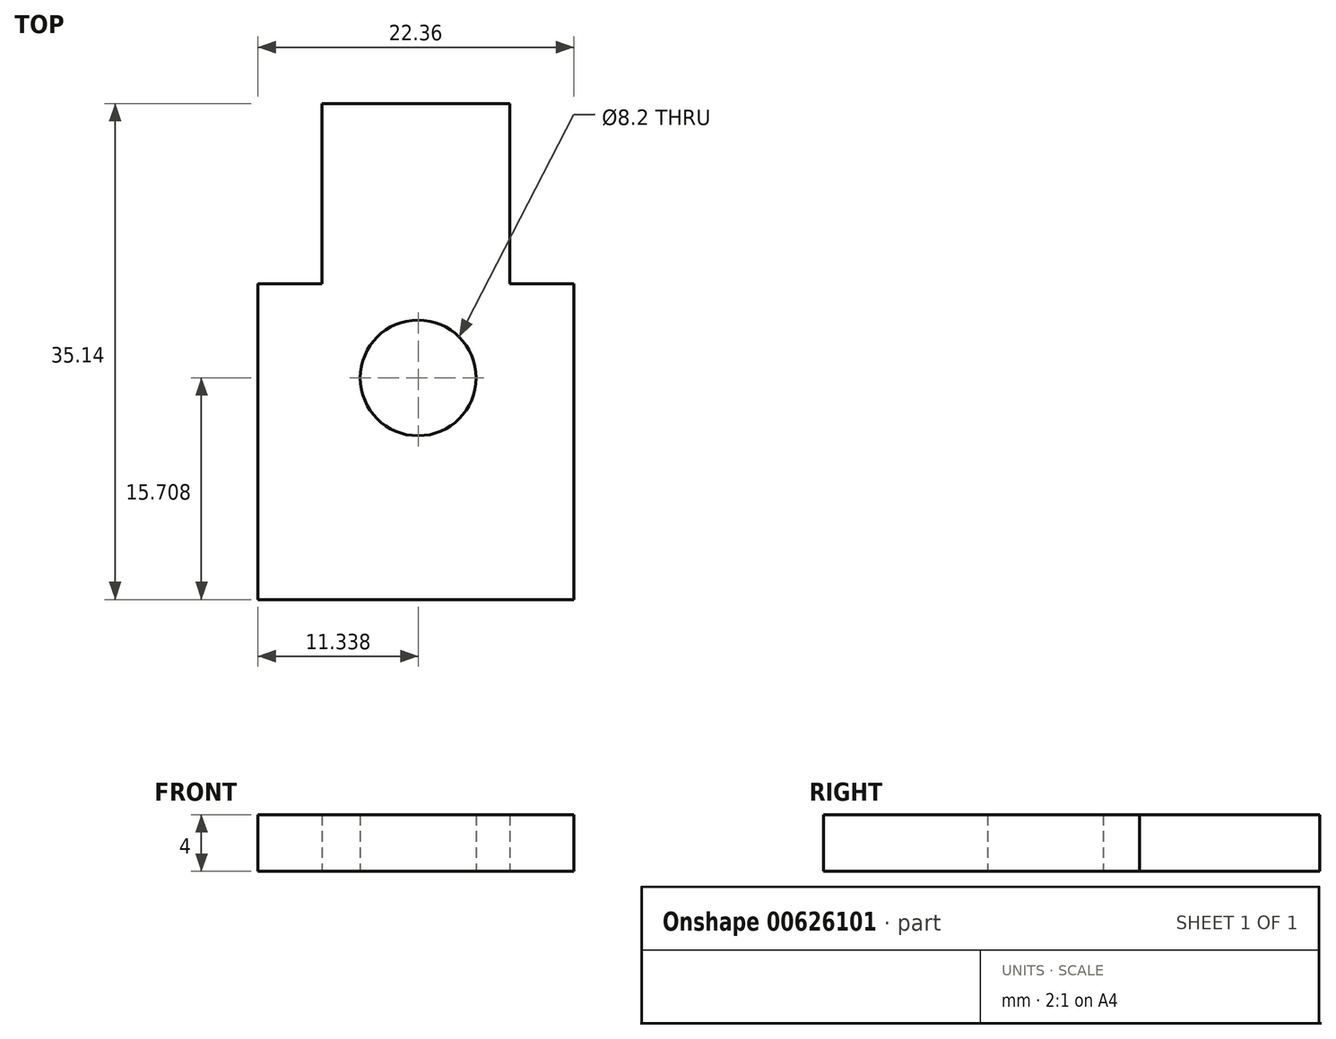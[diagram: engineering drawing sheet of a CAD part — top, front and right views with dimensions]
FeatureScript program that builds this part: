
annotation { "Feature Type Name" : "Feature", "Feature Type Description" : "" }
export const myFeature = defineFeature(function(context is Context, id is Id, definition is map)
    precondition{}
    {
        {
            var Q0;
            Q0=qCreatedBy(makeId("Top.planeOp"),FACE);
            var sketch = newSketch(context, id + "F0", { "sketchPlane" : qUnion([Q0])});
            skLineSegment(sketch, "E0", {"start": v(0, 0) * mm, "end": v(-22.36, 0) * mm});
            skLineSegment(sketch, "E1", {"start": v(0, 0) * mm, "end": v(0, 22.36) * mm});
            skLineSegment(sketch, "E2", {"start": v(-22.36, 0) * mm, "end": v(-22.36, 22.36) * mm});
            skLineSegment(sketch, "E3", {"start": v(-22.36, 22.36) * mm, "end": v(-17.84, 22.36) * mm});
            skLineSegment(sketch, "E4", {"start": v(0, 22.36) * mm, "end": v(-4.53, 22.36) * mm});
            skLineSegment(sketch, "E5", {"start": v(-17.84, 22.36) * mm, "end": v(-17.84, 35.14) * mm});
            skLineSegment(sketch, "E6", {"start": v(-4.53, 22.36) * mm, "end": v(-4.53, 35.14) * mm});
            skLineSegment(sketch, "E7", {"start": v(-17.84, 35.14) * mm, "end": v(-4.53, 35.14) * mm});
            skCircle(sketch, "E8", {"center": v(-11.02, 15.7) * mm, "radius": 4.1 * mm});
            skSolve(sketch);
        }
        {
            var Q0;
            Q0=makeQuery(id+"F0.imprint","IMPRINT",FACE,{"disambiguationData":[TD([[makeQuery(id+"F0.imprint","IMPRINT",EDGE,{"derivedFrom":sQuery(id+"F0.wireOp",EDGE,"E0")}),-1.0]])]});
            extrude(context, id + "F1", {"entities" : qUnion([Q0]), "depth" : 4 * mm, "offsetDistance" : 25 * mm});
        }
    });
